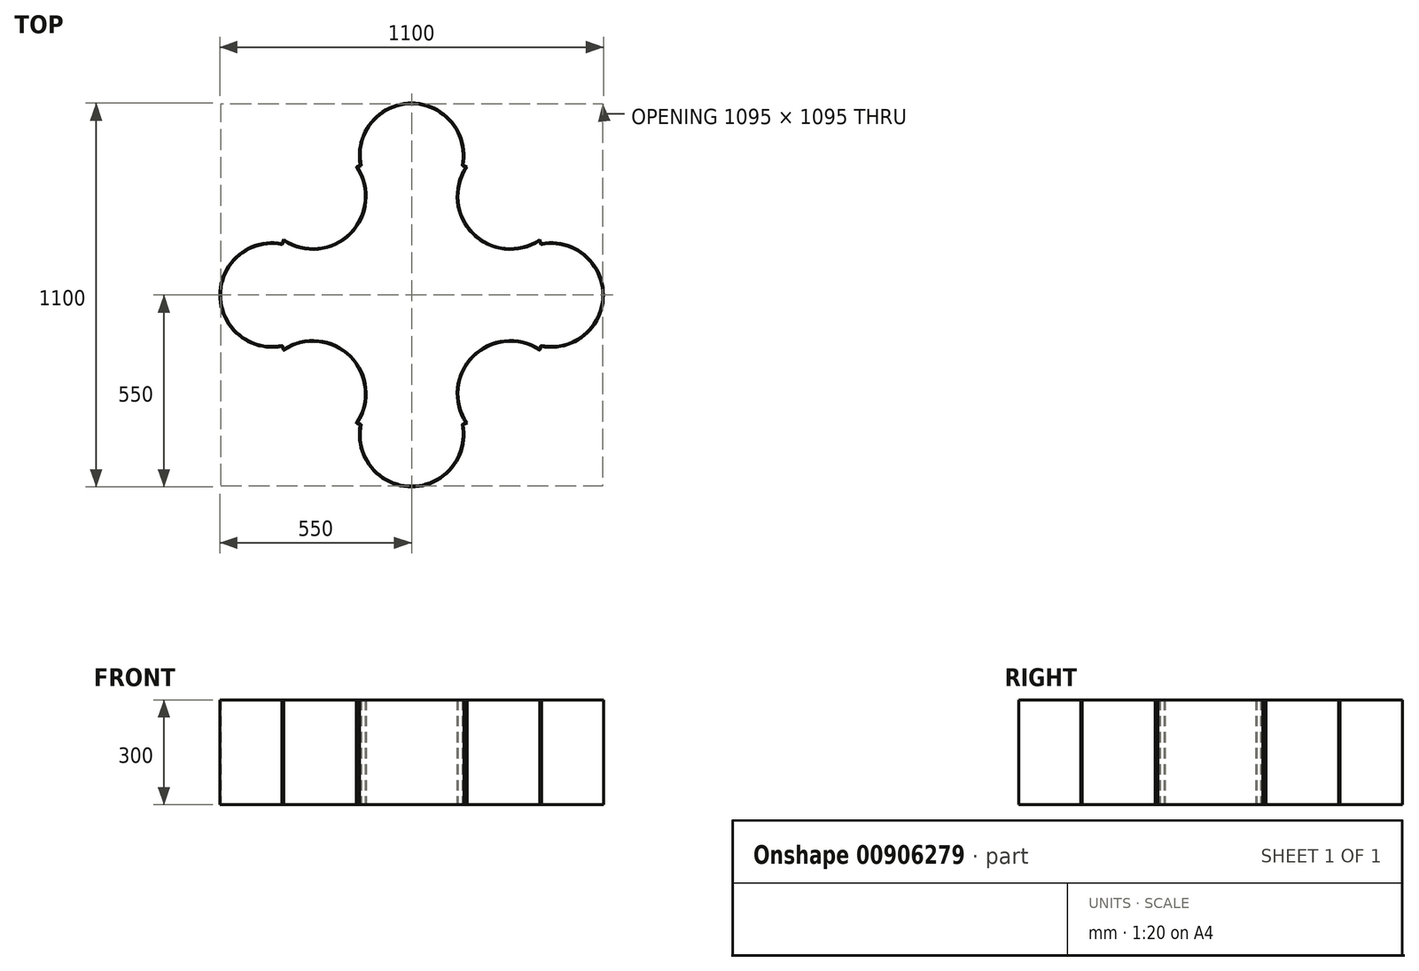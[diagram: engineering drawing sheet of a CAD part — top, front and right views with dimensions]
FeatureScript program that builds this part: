
annotation { "Feature Type Name" : "Feature", "Feature Type Description" : "" }
export const myFeature = defineFeature(function(context is Context, id is Id, definition is map)
    precondition{}
    {
        {
            var Q0;
            Q0=qCreatedBy(makeId("Top.planeOp"),FACE);
            var sketch = newSketch(context, id + "F0", { "sketchPlane" : qUnion([Q0])});
            skArc(sketch, "E0", {"start": v(-367.14, 158.77) * mm, "mid": v(-369.55, 153.07) * mm, "end": v(-371.88, 147.34) * mm});
            skArc(sketch, "E1", {"start": v(147.34, 371.87) * mm, "mid": v(0, 550) * mm, "end": v(-147.34, 371.88) * mm});
            skArc(sketch, "E2", {"start": v(-367.14, 158.77) * mm, "mid": v(-176.78, 176.78) * mm, "end": v(-158.77, 367.14) * mm});
            skArc(sketch, "E3", {"start": v(-371.88, 147.34) * mm, "mid": v(-550, 0) * mm, "end": v(-371.88, -147.34) * mm});
            skArc(sketch, "E4", {"start": v(-158.77, -367.14) * mm, "mid": v(-176.78, -176.78) * mm, "end": v(-367.14, -158.77) * mm});
            skArc(sketch, "E5", {"start": v(-147.34, -371.88) * mm, "mid": v(0, -550) * mm, "end": v(147.34, -371.87) * mm});
            skArc(sketch, "E6", {"start": v(367.14, -158.77) * mm, "mid": v(176.78, -176.78) * mm, "end": v(158.77, -367.14) * mm});
            skArc(sketch, "E7", {"start": v(371.87, -147.34) * mm, "mid": v(550, 0) * mm, "end": v(371.88, 147.34) * mm});
            skArc(sketch, "E8", {"start": v(158.77, 367.14) * mm, "mid": v(176.78, 176.78) * mm, "end": v(367.14, 158.77) * mm});
            skArc(sketch, "E9.trimOffspring", {"start": v(-147.34, 371.88) * mm, "mid": v(-153.07, 369.55) * mm, "end": v(-158.77, 367.14) * mm});
            skArc(sketch, "E10.trimOffspring", {"start": v(158.77, 367.14) * mm, "mid": v(153.07, 369.55) * mm, "end": v(147.34, 371.87) * mm});
            skArc(sketch, "E11.trimOffspring", {"start": v(-158.77, -367.14) * mm, "mid": v(-153.07, -369.55) * mm, "end": v(-147.34, -371.88) * mm});
            skArc(sketch, "E12.trimOffspring", {"start": v(367.14, -158.77) * mm, "mid": v(369.55, -153.07) * mm, "end": v(371.88, -147.34) * mm});
            skArc(sketch, "E13.trimOffspring", {"start": v(147.34, -371.87) * mm, "mid": v(153.07, -369.55) * mm, "end": v(158.77, -367.14) * mm});
            skArc(sketch, "E14.trimOffspring", {"start": v(371.88, 147.34) * mm, "mid": v(369.55, 153.07) * mm, "end": v(367.14, 158.77) * mm});
            skArc(sketch, "E15.trimOffspring", {"start": v(-371.88, -147.34) * mm, "mid": v(-369.55, -153.07) * mm, "end": v(-367.14, -158.77) * mm});
            skSolve(sketch);
        }
        {
            var Q0;
            Q0=makeQuery(id+"F0.imprint","IMPRINT",FACE,{"disambiguationData":[TD([[makeQuery(id+"F0.imprint","IMPRINT",EDGE,{"derivedFrom":sQuery(id+"F0.wireOp",EDGE,"E0")}),1.0]])]});
            extrude(context, id + "F1", {"entities" : qUnion([Q0]), "depth" : 300 * mm, "offsetDistance" : 25 * mm});
        }
        {
            var Q0;
            Q0=makeQuery(id+"F1.opExtrude","CAP_FACE",FACE,{"disambiguationData":[OSD([sQuery(id+"F0.wireOp",EDGE,"E0"),sQuery(id+"F0.wireOp",EDGE,"E1"),sQuery(id+"F0.wireOp",EDGE,"E2"),sQuery(id+"F0.wireOp",EDGE,"E3"),sQuery(id+"F0.wireOp",EDGE,"E4"),sQuery(id+"F0.wireOp",EDGE,"E5"),sQuery(id+"F0.wireOp",EDGE,"E6"),sQuery(id+"F0.wireOp",EDGE,"E7"),sQuery(id+"F0.wireOp",EDGE,"E8"),sQuery(id+"F0.wireOp",EDGE,"E9.trimOffspring"),sQuery(id+"F0.wireOp",EDGE,"E10.trimOffspring"),sQuery(id+"F0.wireOp",EDGE,"E11.trimOffspring"),sQuery(id+"F0.wireOp",EDGE,"E12.trimOffspring"),sQuery(id+"F0.wireOp",EDGE,"E13.trimOffspring"),sQuery(id+"F0.wireOp",EDGE,"E14.trimOffspring"),sQuery(id+"F0.wireOp",EDGE,"E15.trimOffspring")])],"isStart":false});
            var Q1;
            Q1=makeQuery(id+"F1.opExtrude","CAP_FACE",FACE,{"disambiguationData":[OSD([sQuery(id+"F0.wireOp",EDGE,"E0"),sQuery(id+"F0.wireOp",EDGE,"E1"),sQuery(id+"F0.wireOp",EDGE,"E2"),sQuery(id+"F0.wireOp",EDGE,"E3"),sQuery(id+"F0.wireOp",EDGE,"E4"),sQuery(id+"F0.wireOp",EDGE,"E5"),sQuery(id+"F0.wireOp",EDGE,"E6"),sQuery(id+"F0.wireOp",EDGE,"E7"),sQuery(id+"F0.wireOp",EDGE,"E8"),sQuery(id+"F0.wireOp",EDGE,"E9.trimOffspring"),sQuery(id+"F0.wireOp",EDGE,"E10.trimOffspring"),sQuery(id+"F0.wireOp",EDGE,"E11.trimOffspring"),sQuery(id+"F0.wireOp",EDGE,"E12.trimOffspring"),sQuery(id+"F0.wireOp",EDGE,"E13.trimOffspring"),sQuery(id+"F0.wireOp",EDGE,"E14.trimOffspring"),sQuery(id+"F0.wireOp",EDGE,"E15.trimOffspring")])],"isStart":true});
            shell(context, id + "F2", {"entities" : qUnion([Q0, Q1]), "thickness" : 2.5 * mm});
        }
    });
